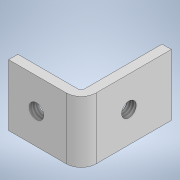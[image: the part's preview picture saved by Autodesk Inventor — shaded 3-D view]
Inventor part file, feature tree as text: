
AUTODESK INVENTOR PART (.ipt)
format: ipt  version: 2021 (Build 250183000, 183)  size: 117,760 bytes
history: native  units: mm
features: sketch x3, hole x2, fillet x2, extrude x1
ambient origin geometry x8: Origin, YZ Plane, XZ Plane, XY Plane, X Axis, Y Axis, Z Axis, Center Point
bodies: Solid1 (feature_tree)
feature tree (8):
  extrude  "Extrusion1"  Depth=12.16mm
  hole  "Hole1"  [1 undecoded]
  hole  "Hole2"  [1 undecoded]
  fillet  "Fillet1"  Radius=2.5mm
  fillet  "Fillet2"  Radius=0.5mm
  sketch  "Sketch1"  dims[d2=1.55mm d3=12.16mm]
  sketch  "Sketch2"  dims[d4=15.12mm d5=10.3mm d6=0.0mm]
  sketch  "Sketch3"  dims[d7=7.5mm d8=2.459mm d9=6.0mm d10=4.0mm d11=2.0mm d12=90.0deg d13=8.8mm d14=20.594885mm d15=8.0mm d16=2.459mm d17=6.0mm d18=4.0mm d19=2.0mm d20=90.0deg d21=8.8mm d22=20.594885mm d23=2.5mm d24=0.5mm]
note: 2 required parameter values undecoded (feature->parameter linkage not recoverable at this tier; creation-order binding heuristic only, values carry confidence <= 0.55)
